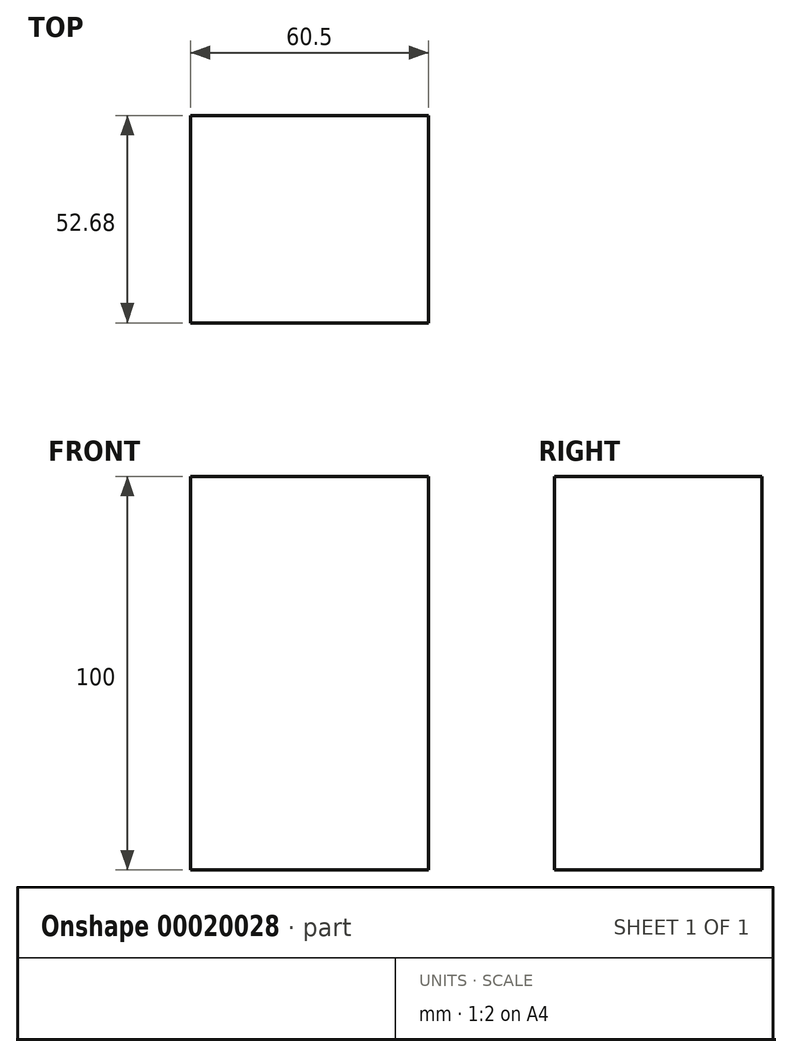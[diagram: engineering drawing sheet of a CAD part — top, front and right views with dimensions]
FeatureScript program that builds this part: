
annotation { "Feature Type Name" : "Feature", "Feature Type Description" : "" }
export const myFeature = defineFeature(function(context is Context, id is Id, definition is map)
    precondition{}
    {
        {
            var Q0;
            Q0=qCreatedBy(makeId("Top.planeOp"),FACE);
            var sketch = newSketch(context, id + "F0", { "sketchPlane" : qUnion([Q0])});
            skLineSegment(sketch, "E0.rect.bottom", {"start": v(30.25, -26.34) * mm, "end": v(-30.25, -26.34) * mm});
            skLineSegment(sketch, "E0.rect.top", {"start": v(30.25, 26.34) * mm, "end": v(-30.25, 26.34) * mm});
            skLineSegment(sketch, "E0.rect.left", {"start": v(30.25, -26.34) * mm, "end": v(30.25, 26.34) * mm});
            skLineSegment(sketch, "E0.rect.right", {"start": v(-30.25, -26.34) * mm, "end": v(-30.25, 26.34) * mm});
            skPoint(sketch, "E0.rect.middle", {"position": v(0, 0) * mm});
            skSolve(sketch);
        }
        {
            var Q0;
            Q0 = qSketchRegion(id + "F0", true);
            var Q1;
            Q1=makeQuery(id+"F0.imprint","IMPRINT",FACE,{"disambiguationData":[TD([[makeQuery(id+"F0.imprint","IMPRINT",EDGE,{"derivedFrom":sQuery(id+"F0.wireOp",EDGE,"E0.rect.bottom")}),-1.0]])]});
            extrude(context, id + "F1", {"entities" : qUnion([Q0, Q1]), "depth" : 100 * mm});
        }
    });
